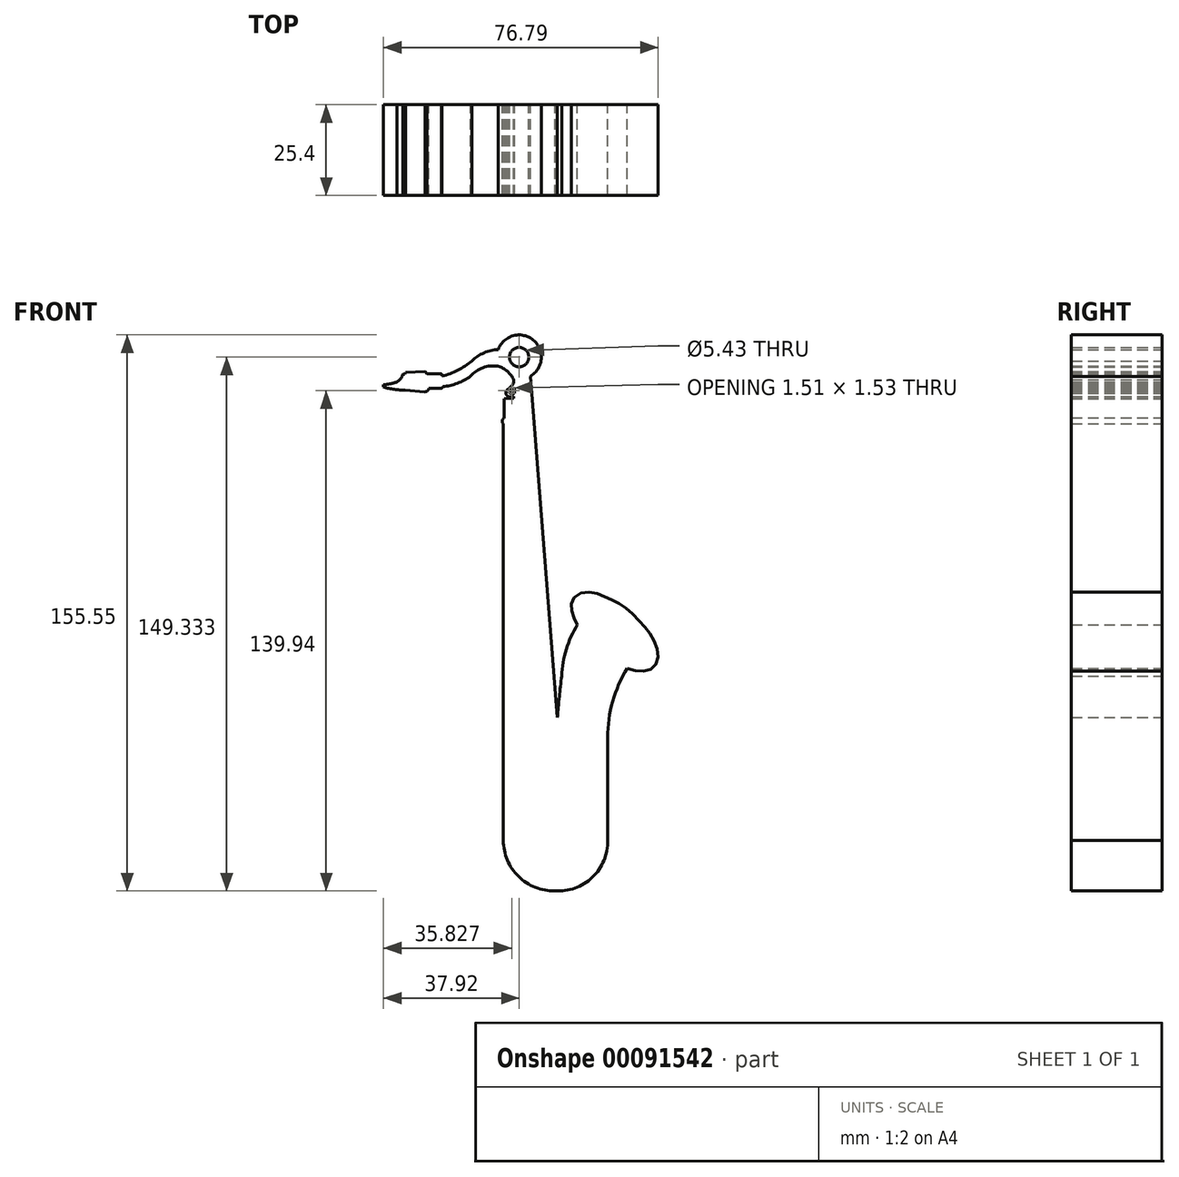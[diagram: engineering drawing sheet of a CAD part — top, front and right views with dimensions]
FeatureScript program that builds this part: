
annotation { "Feature Type Name" : "Feature", "Feature Type Description" : "" }
export const myFeature = defineFeature(function(context is Context, id is Id, definition is map)
    precondition{}
    {
        {
            var Q0;
            Q0=qCreatedBy(makeId("Front.planeOp"),FACE);
            var sketch = newSketch(context, id + "F0", { "sketchPlane" : qUnion([Q0])});
            skArc(sketch, "E0", {"start": v(-23, 68.12) * mm, "mid": v(-25, 68.23) * mm, "end": v(-27.02, 68.17) * mm});
            skArc(sketch, "E1", {"start": v(-22.77, 67.49) * mm, "mid": v(-22.8, 67.84) * mm, "end": v(-23, 68.12) * mm});
            skArc(sketch, "E2", {"start": v(-22.77, 67.49) * mm, "mid": v(-18.36, 69.15) * mm, "end": v(-14.45, 71.78) * mm});
            skArc(sketch, "E3", {"start": v(-7.09, 74.94) * mm, "mid": v(-11.06, 74.04) * mm, "end": v(-14.45, 71.78) * mm});
            skLineSegment(sketch, "E4", {"start": v(-27.02, 68.17) * mm, "end": v(-27.5, 68.85) * mm});
            skLineSegment(sketch, "E5", {"start": v(-27.5, 68.85) * mm, "end": v(-32.94, 68.51) * mm});
            skLineSegment(sketch, "E6", {"start": v(-32.94, 68.51) * mm, "end": v(-33.28, 68.1) * mm});
            skLineSegment(sketch, "E7", {"start": v(-33.28, 68.1) * mm, "end": v(-33.77, 68.1) * mm});
            skArc(sketch, "E8", {"start": v(-35.44, 65.9) * mm, "mid": v(-34.35, 66.8) * mm, "end": v(-33.77, 68.1) * mm});
            skArc(sketch, "E9", {"start": v(-39.14, 65.12) * mm, "mid": v(-37.26, 65.39) * mm, "end": v(-35.44, 65.9) * mm});
            skLineSegment(sketch, "E10", {"start": v(-39.14, 65.12) * mm, "end": v(-39.14, 64.44) * mm});
            skArc(sketch, "E11", {"start": v(-39.14, 64.44) * mm, "mid": v(-36.16, 63.82) * mm, "end": v(-33.13, 63.57) * mm});
            skLineSegment(sketch, "E12", {"start": v(-33.13, 63.57) * mm, "end": v(-27.68, 63.16) * mm});
            skArc(sketch, "E13", {"start": v(-27.68, 63.16) * mm, "mid": v(-26.87, 63.4) * mm, "end": v(-26.44, 64.12) * mm});
            skLineSegment(sketch, "E14", {"start": v(-26.44, 64.12) * mm, "end": v(-23, 64.12) * mm});
            skArc(sketch, "E15", {"start": v(-23, 64.12) * mm, "mid": v(-22.68, 64.25) * mm, "end": v(-22.56, 64.57) * mm});
            skArc(sketch, "E16", {"start": v(-22.56, 64.57) * mm, "mid": v(-18.49, 65.51) * mm, "end": v(-14.8, 67.48) * mm});
            skArc(sketch, "E17", {"start": v(-7.15, 70.3) * mm, "mid": v(-11.34, 69.87) * mm, "end": v(-14.8, 67.48) * mm});
            skArc(sketch, "E18", {"start": v(-2.77, 66.48) * mm, "mid": v(-4.53, 68.89) * mm, "end": v(-7.15, 70.3) * mm});
            skLineSegment(sketch, "E19", {"start": v(-2.77, 66.48) * mm, "end": v(-2.77, 65.47) * mm});
            skArc(sketch, "E20", {"start": v(-4.4, 63.81) * mm, "mid": v(-3.53, 64.58) * mm, "end": v(-2.77, 65.47) * mm});
            skArc(sketch, "E21", {"start": v(-4.4, 63.81) * mm, "mid": v(-4.93, 62.85) * mm, "end": v(-4.4, 61.9) * mm});
            skArc(sketch, "E22", {"start": v(-4.4, 61.9) * mm, "mid": v(-3.58, 61.7) * mm, "end": v(-2.76, 61.9) * mm});
            skLineSegment(sketch, "E23", {"start": v(-2.56, 64.21) * mm, "end": v(-2.56, 62.77) * mm});
            skArc(sketch, "E24", {"start": v(-4.07, 62.85) * mm, "mid": v(-3.32, 62.69) * mm, "end": v(-2.56, 62.77) * mm});
            skArc(sketch, "E25", {"start": v(-2.56, 64.21) * mm, "mid": v(-3.38, 63.6) * mm, "end": v(-4.07, 62.85) * mm});
            skLineSegment(sketch, "E26", {"start": v(-2.76, 61.9) * mm, "end": v(-2.76, 61.3) * mm});
            skLineSegment(sketch, "E27", {"start": v(-2.76, 61.3) * mm, "end": v(-5.36, 61.2) * mm});
            skLineSegment(sketch, "E28", {"start": v(-5.36, 61.2) * mm, "end": v(-5.36, 55.82) * mm});
            skArc(sketch, "E29", {"start": v(-5.36, 55.82) * mm, "mid": v(-5.96, 55.06) * mm, "end": v(-5.62, 54.15) * mm});
            skLineSegment(sketch, "E30", {"start": v(-5.62, 54.15) * mm, "end": v(-5.62, -62.38) * mm});
            skArc(sketch, "E31", {"start": v(-5.62, -62.38) * mm, "mid": v(-1.4, -72.44) * mm, "end": v(8.75, -76.45) * mm});
            skArc(sketch, "E32", {"start": v(8.75, -76.45) * mm, "mid": v(19.27, -72.7) * mm, "end": v(23.54, -62.38) * mm});
            skLineSegment(sketch, "E33", {"start": v(23.54, -62.38) * mm, "end": v(23.54, -33.6) * mm});
            skArc(sketch, "E34", {"start": v(29.02, -14.2) * mm, "mid": v(24.93, -23.52) * mm, "end": v(23.54, -33.6) * mm});
            skFitSpline(sketch, "E35", {"points": [v(29.02, -14.2) * mm, v(33, -15) * mm, v(36.08, -14.2) * mm, v(37.58, -11.73) * mm, v(37.05, -7.76) * mm, v(35.1, -4.05) * mm, v(32.37, -0.97) * mm, v(29.02, 2.38) * mm, v(25.58, 4.41) * mm, v(22.32, 6) * mm, v(18.8, 7.06) * mm, v(14.9, 6.26) * mm, v(13.41, 3.8) * mm, v(13.76, 0.97) * mm, v(15.09, -2.03) * mm, v(17.82, -5.82) * mm, v(22.23, -9.88) * mm, v(25.93, -12.6) * mm, v(29.02, -14.2) * mm]});
            skArc(sketch, "E36", {"start": v(15.09, -2.03) * mm, "mid": v(11.96, -8.91) * mm, "end": v(10.65, -16.36) * mm});
            skLineSegment(sketch, "E37", {"start": v(1.93, 67.47) * mm, "end": v(9.48, -28) * mm});
            skArc(sketch, "E38", {"start": v(10.65, -16.36) * mm, "mid": v(10.03, -22.18) * mm, "end": v(9.48, -28) * mm});
            skCircle(sketch, "E39", {"center": v(-1.22, 72.84) * mm, "radius": 2.71 * mm});
            skArc(sketch, "E40", {"start": v(1.93, 67.47) * mm, "mid": v(2.74, 77.62) * mm, "end": v(-7.09, 74.94) * mm});
            skSolve(sketch);
        }
        {
            var Q0;
            Q0 = qSketchRegion(id + "F0", true);
            extrude(context, id + "F1", {"entities" : qUnion([Q0]), "depth" : 25.4 * mm});
        }
    });
